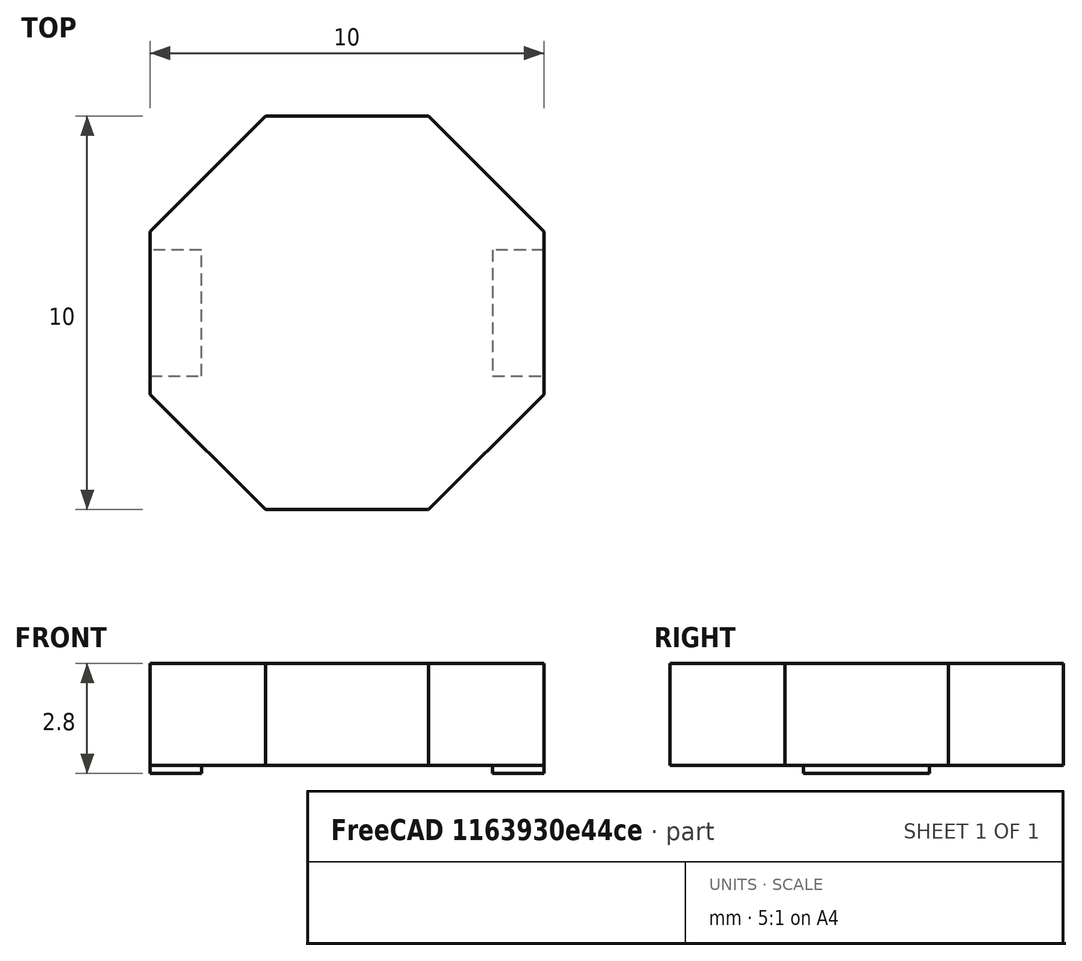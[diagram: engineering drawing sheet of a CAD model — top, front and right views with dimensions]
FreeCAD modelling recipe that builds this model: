
FCSTD DOCUMENT  (FreeCAD 0.16RUnknown)
Label: SRU1028
License: All rights reserved
LicenseURL: http://en.wikipedia.org/wiki/All_rights_reserved
objects: Part::Part2DObjectPython×3, Part::Extrusion×3
note: 6 computed .brp shape members not serialized (recipe doc carries the construction recipe); baked Part::Feature solids carry a one-line shape summary decoded from their .brp

FEATURE [Part::Part2DObjectPython] Polygon  # Draft 2D object (typed FeaturePython)
  ChamferSize = 0
  DrawMode = 1
  FacesNumber = 8
  FilletRadius = 0
  MakeFace = true
  Placement = pos=(0,0,0.2) rot=(0,0,1;0.392699rad)
  Radius = 5
FEATURE [Part::Part2DObjectPython] Rectangle  # Draft 2D object (typed FeaturePython)
  ChamferSize = 0
  Columns = 1
  FilletRadius = 0
  Height = 3.2
  Length = 1.3
  MakeFace = true
  Placement = pos=(-5,-1.6,0) rot=(0,0,1;0rad)
  Rows = 1
FEATURE [Part::Part2DObjectPython] Rectangle001  # Draft 2D object (typed FeaturePython)
  ChamferSize = 0
  Columns = 1
  FilletRadius = 0
  Height = 3.2
  Length = 1.3
  MakeFace = true
  Placement = pos=(3.7,-1.6,0) rot=(0,0,1;0rad)
  Rows = 1
FEATURE [Part::Extrusion] Extrude
  Base = -> Rectangle
  Dir = (0,0,0.2)
  Solid = false
FEATURE [Part::Extrusion] Extrude001
  Base = -> Rectangle001
  Dir = (0,0,0.2)
  Solid = false
FEATURE [Part::Extrusion] Extrude003
  Base = -> Polygon
  Dir = (0,0,2.6)
  Solid = false
